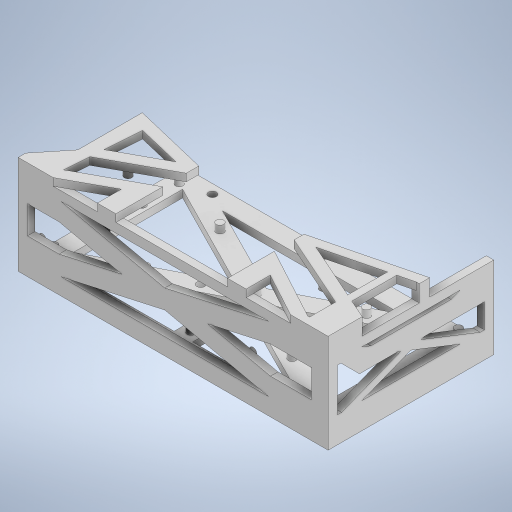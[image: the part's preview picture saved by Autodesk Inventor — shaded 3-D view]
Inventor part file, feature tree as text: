
AUTODESK INVENTOR PART (.ipt)
format: ipt  version: 2024 (Build 280153000, 153)  size: 843,776 bytes
history: native  units: in
note: dims shown in document units (in); Inventor stores cm internally (conversion verified against a paired STEP export)
features: extrude x28, sketch x28, fillet x1
ambient origin geometry x8: Origin, YZ Plane, XZ Plane, XY Plane, X Axis, Y Axis, Z Axis, Center Point
bodies: Solid1 (feature_tree)
feature tree (57):
  extrude  "Extrusion1"  Depth=4.0in
  extrude  "Extrusion2"  Depth=0.25in
  extrude  "Extrusion3"  Depth=0.625in TaperAngle=0.0deg
  extrude  "Extrusion4"  Depth=3.375in
  extrude  "Extrusion5"  Depth=7.375in
  extrude  "Extrusion6"  Depth=0.2in
  extrude  "Extrusion7"  Depth=0.2in
  extrude  "Extrusion8"  Depth=0.2in
  extrude  "Extrusion9"  Depth=0.2in
  extrude  "Extrusion10"  Depth=0.2in
  extrude  "Extrusion11"  Depth=0.2in
  extrude  "Extrusion12"  Depth=0.2in
  extrude  "Extrusion13"  Depth=0.2in
  extrude  "Extrusion14"  Depth=0.25in TaperAngle=0.0deg
  extrude  "Extrusion15"  Depth=0.2in
  extrude  "Extrusion16"  Depth=0.5in TaperAngle=0.0deg
  extrude  "Extrusion17"  Depth=0.2in TaperAngle=0.0deg
  extrude  "Extrusion18"  Depth=0.2in TaperAngle=0.0deg
  fillet  "Fillet1"  Radius=1.0in
  extrude  "Extrusion19"  Depth=7.375in
  extrude  "Extrusion20"  Depth=0.2in
  extrude  "Extrusion21"  Depth=0.2in
  extrude  "Extrusion22"  Depth=0.2in
  extrude  "Extrusion23"  Depth=0.2in
  extrude  "Extrusion24"  Depth=0.2in
  extrude  "Extrusion25"  Depth=0.2in
  extrude  "Extrusion26"  Depth=0.2in TaperAngle=0.0deg
  extrude  "Extrusion27"  Depth=1.0in TaperAngle=0.0deg
  extrude  "Extrusion28"  Depth=0.5in
  sketch  "Sketch1"  dims[d0=7.0in d1=4.0in]
  sketch  "Sketch2"  dims[d2=1.75in d3=0.0in d4=0.25in]
  sketch  "Sketch3"  dims[d5=0.625in d6=0.0625in d7=0.0in]
  sketch  "Sketch4"  dims[d8=0.0625in d9=0.0in d10=3.375in]
  sketch  "Sketch5"  dims[d11=0.5in d12=0.0in d13=7.375in]
  sketch  "Sketch6"  dims[d14=1.25in d15=0.2in]
  sketch  "Sketch7"  dims[d16=0.2in d17=0.2in]
  sketch  "Sketch8"  dims[d18=0.2in d19=0.2in]
  sketch  "Sketch9"  dims[d20=0.2in d21=0.2in]
  sketch  "Sketch10"  dims[d22=0.2in d23=0.2in]
  sketch  "Sketch11"  dims[d24=0.25in d25=0.0in d26=0.2in]
  sketch  "Sketch12"  dims[d27=0.2in d28=0.2in]
  sketch  "Sketch13"  dims[d29=0.2in d30=0.2in]
  sketch  "Sketch14"  dims[d31=0.2in d32=0.25in d33=0.0in]
  sketch  "Sketch15"  dims[d34=0.2in d35=0.2in]
  sketch  "Sketch16"  dims[d36=0.2in d37=0.5in d38=0.0in]
  sketch  "Sketch17"  dims[d39=0.2in d40=0.0in d41=0.2in d42=0.0in]
  sketch  "Sketch18"  dims[d43=0.2in d44=0.0in d45=0.2in d46=0.0in d47=1.0in d48=0.0in]
  sketch  "Sketch19"  dims[d49=1.0in d50=0.0in d51=7.375in]
  sketch  "Sketch20"  dims[d52=3.5in d53=0.2in]
  sketch  "Sketch21"  dims[d54=0.2in d55=0.2in]
  sketch  "Sketch22"  dims[d56=0.2in d57=0.2in]
  sketch  "Sketch23"  dims[d58=0.2in d59=0.2in]
  sketch  "Sketch24"  dims[d60=0.2in d61=0.2in]
  sketch  "Sketch25"  dims[d62=0.2in d63=0.2in]
  sketch  "Sketch26"  dims[d64=0.25in d65=0.0in d66=0.2in d67=0.0in]
  sketch  "Sketch27"  dims[d68=0.2in d69=0.0in d70=1.0in d71=0.0in]
  sketch  "Sketch28"  dims[d72=0.25in d73=0.5in d74=0.25in d75=0.25in d76=0.25in d77=0.25in d78=0.5in d79=0.5in d80=0.25in d81=0.25in d82=0.25in d83=0.25in d84=0.0in d85=0.125in d86=0.1in d87=0.1in d88=0.1in d89=0.1in d90=0.25in d91=0.25in d92=3.95in d93=1.25in d94=45.0deg d95=0.25in d96=0.25in d97=0.25in d98=0.25in d99=0.25in d100=0.25in d101=0.25in d102=0.25in d103=0.2in d104=0.0in d106=0.25in d107=0.25in d108=0.1in d109=0.1in d110=0.15in d111=0.15in d112=0.15in d113=0.15in d114=0.25in d115=0.15in d116=0.15in d117=0.25in d118=0.15in d119=0.15in d120=0.15in d121=0.5in d122=0.25in d123=0.2in d124=0.0in d125=1.0in d126=0.0in d127=4.1in d128=1.85in d129=7.675in d130=0.0in d131=0.05in d132=7.675in d133=0.0in d134=0.25in d135=1.0in d136=0.0in d137=0.21in d138=0.21in d139=0.21in d140=0.21in d141=1.0in d142=0.0in d143=1.0in d144=0.0in d145=1.0in d146=0.0in d147=0.2in d148=0.0in]
